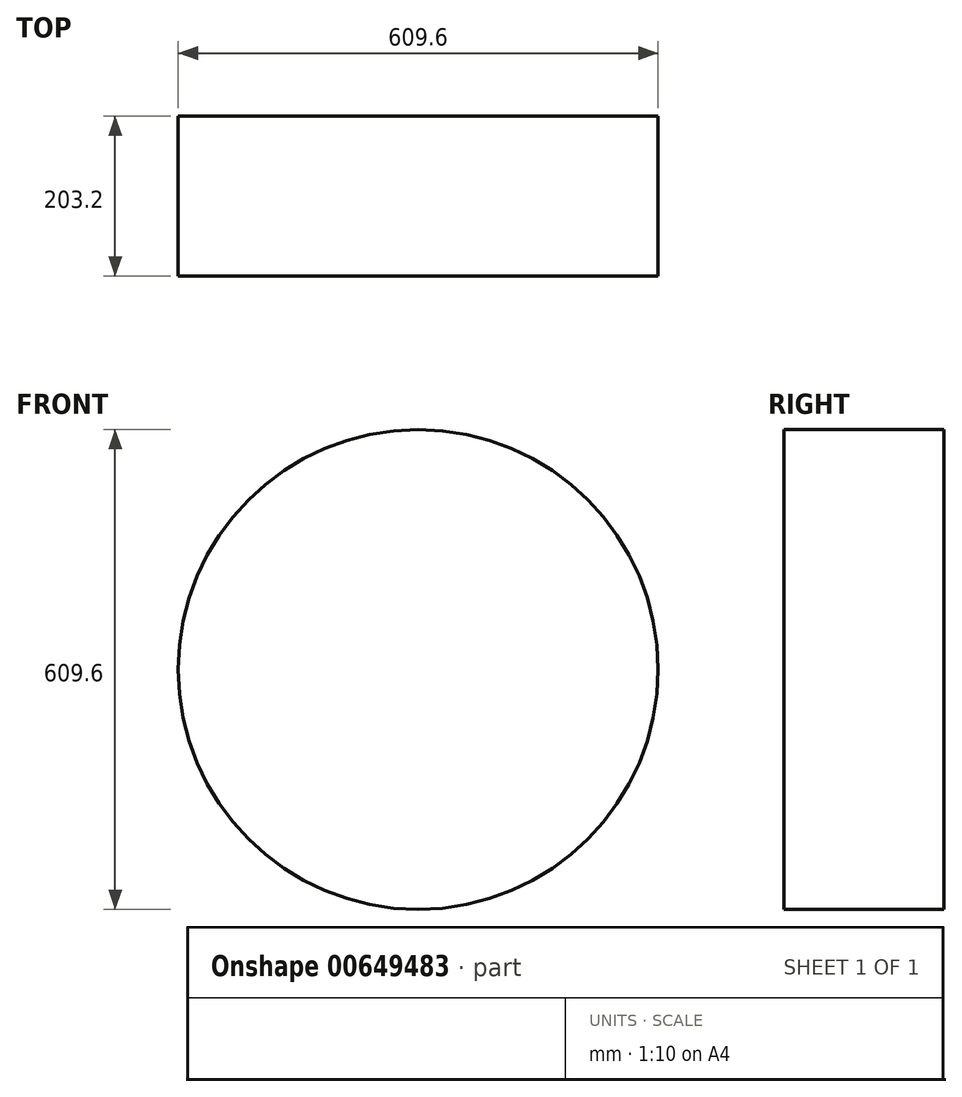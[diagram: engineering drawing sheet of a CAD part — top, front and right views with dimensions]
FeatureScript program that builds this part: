
annotation { "Feature Type Name" : "Feature", "Feature Type Description" : "" }
export const myFeature = defineFeature(function(context is Context, id is Id, definition is map)
    precondition{}
    {
        {
            var Q0;
            Q0=qCreatedBy(makeId("Front.planeOp"),FACE);
            var sketch = newSketch(context, id + "F0", { "sketchPlane" : qUnion([Q0])});
            skCircle(sketch, "E0", {"center": v(0, 0) * mm, "radius": 304.8 * mm});
            skSolve(sketch);
        }
        {
            var Q0;
            Q0=makeQuery(id+"F0.imprint","IMPRINT",FACE,{"disambiguationData":[TD([[makeQuery(id+"F0.imprint","IMPRINT",EDGE,{"derivedFrom":sQuery(id+"F0.wireOp",EDGE,"E0")}),1.0]])]});
            extrude(context, id + "F1", {"entities" : qUnion([Q0]), "depth" : 203.2 * mm, "offsetDistance" : 25.4 * mm});
        }
        {
            var Q0;
            Q0=makeQuery(id+"F1.opExtrude","CAP_FACE",FACE,{"disambiguationData":[OSD([sQuery(id+"F0.wireOp",EDGE,"E0")])],"isStart":false});
            var sketch = newSketch(context, id + "F2", { "sketchPlane" : qUnion([Q0])});
            skLineSegment(sketch, "E1", {"start": v(0, 0) * mm, "end": v(0, 133.21) * mm});
            skLineSegment(sketch, "E2", {"start": v(0, 0) * mm, "end": v(158.87, 0) * mm});
            skSolve(sketch);
        }
    });
